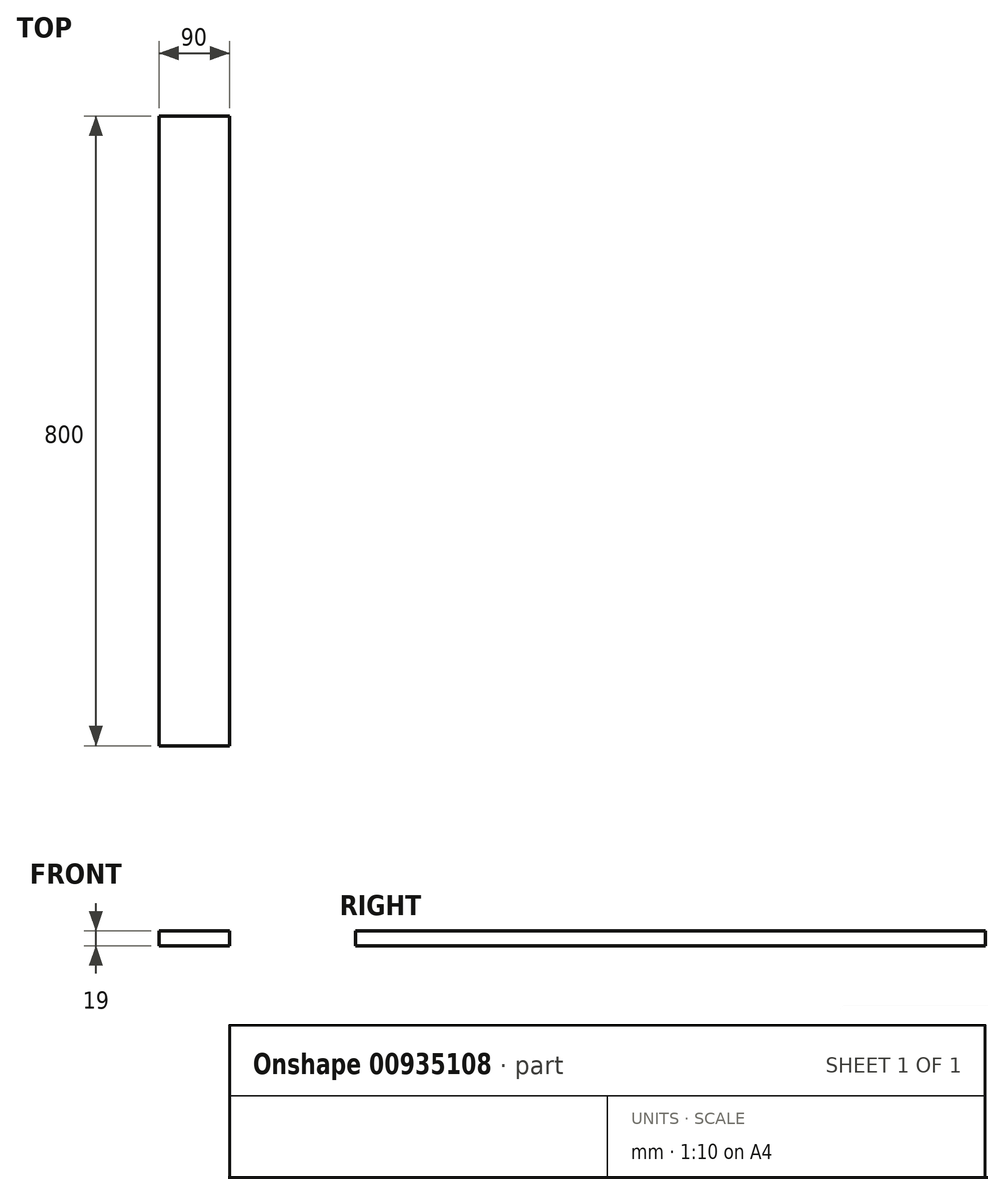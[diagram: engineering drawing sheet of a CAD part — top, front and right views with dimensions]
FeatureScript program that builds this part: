
annotation { "Feature Type Name" : "Feature", "Feature Type Description" : "" }
export const myFeature = defineFeature(function(context is Context, id is Id, definition is map)
    precondition{}
    {
        {
            var Q0;
            Q0=qCreatedBy(makeId("Front.planeOp"),FACE);
            var sketch = newSketch(context, id + "F0", { "sketchPlane" : qUnion([Q0])});
            skLineSegment(sketch, "E0.bottom", {"start": v(0, 0) * mm, "end": v(90, 0) * mm});
            skLineSegment(sketch, "E0.top", {"start": v(0, 19) * mm, "end": v(90, 19) * mm});
            skLineSegment(sketch, "E0.left", {"start": v(0, 0) * mm, "end": v(0, 19) * mm});
            skLineSegment(sketch, "E0.right", {"start": v(90, 0) * mm, "end": v(90, 19) * mm});
            skSolve(sketch);
        }
        {
            var Q0;
            Q0=makeQuery(id+"F0.imprint","IMPRINT",FACE,{"disambiguationData":[TD([[makeQuery(id+"F0.imprint","IMPRINT",EDGE,{"derivedFrom":sQuery(id+"F0.wireOp",EDGE,"E0.bottom")}),1.0]])]});
            extrude(context, id + "F1", {"entities" : qUnion([Q0]), "depth" : 800 * mm, "offsetDistance" : 25 * mm});
        }
    });
